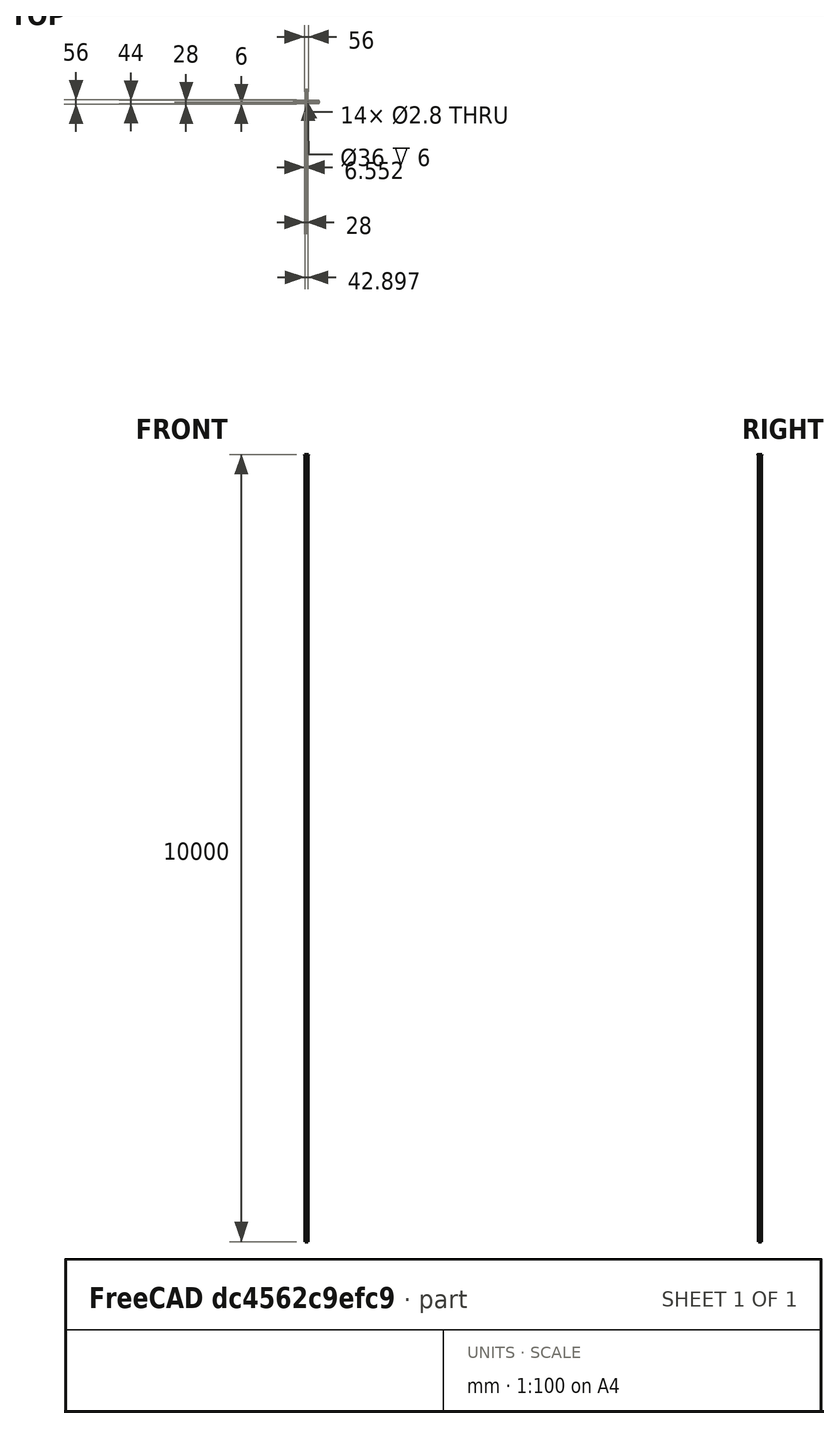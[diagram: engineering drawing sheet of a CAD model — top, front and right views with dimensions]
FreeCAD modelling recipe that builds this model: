
FCSTD DOCUMENT  (FreeCAD 0.16R)
Label: SpokeHoles52mm-28h
License: All rights reserved
LicenseURL: http://en.wikipedia.org/wiki/All_rights_reserved
objects: Sketcher::SketchObject×3, PartDesign::Pocket×3, PartDesign::Pad×1, PartDesign::PolarPattern×1, Mesh::Feature×1
note: 12 computed .brp shape members not serialized (recipe doc carries the construction recipe); baked Part::Feature solids carry a one-line shape summary decoded from their .brp

FEATURE [Sketcher::SketchObject] Sketch
  sketch-geometry (1):
    g0: Circle CenterX=0 CenterY=0 CenterZ=0 NormalX=0 NormalY=0 NormalZ=1 Radius=28
  constraints (2):
    c: Radius(g0) = 28
    c: Coincident(g0,g-1)
FEATURE [PartDesign::Pad] Pad
  Length = 6
  Length2 = 100
  Sketch = -> Sketch
  Type = 0
FEATURE [Sketcher::SketchObject] Sketch001
  Placement = pos=(0,0,6) rot=(0,0,1;0rad)
  Support = -> Pad [Face3]
  sketch-geometry (1):
    g0: Circle CenterX=0 CenterY=0 CenterZ=0 NormalX=0 NormalY=0 NormalZ=1 Radius=18
  constraints (2):
    c: Radius(g0) = 18
    c: Coincident(g0,g-1)
FEATURE [PartDesign::Pocket] Pocket
  Length = 5
  Sketch = -> Sketch001
  Type = 1
FEATURE [PartDesign::Pocket] Pocket001
  Length = 5
  Type = 1
FEATURE [PartDesign::PolarPattern] PolarPattern
  Angle = 360
  Occurrences = 14
  Originals = -> [Pocket001]
FEATURE [Sketcher::SketchObject] Sketch004
  Placement = pos=(0,0,0) rot=(1,0,0;3.14159rad)
  Support = -> PolarPattern [Face2]
  sketch-geometry (1):
    g0: Circle CenterX=0 CenterY=0 CenterZ=0 NormalX=0 NormalY=0 NormalZ=1 Radius=26
  constraints (2):
    c: Radius(g0) = 26
    c: Coincident(g0,g-1)
FEATURE [PartDesign::Pocket] Pocket002
  Length = 3
  Sketch = -> Sketch004
  Type = 0
FEATURE [Mesh::Feature] Mesh  label="Pocket002 (Meshed)"
